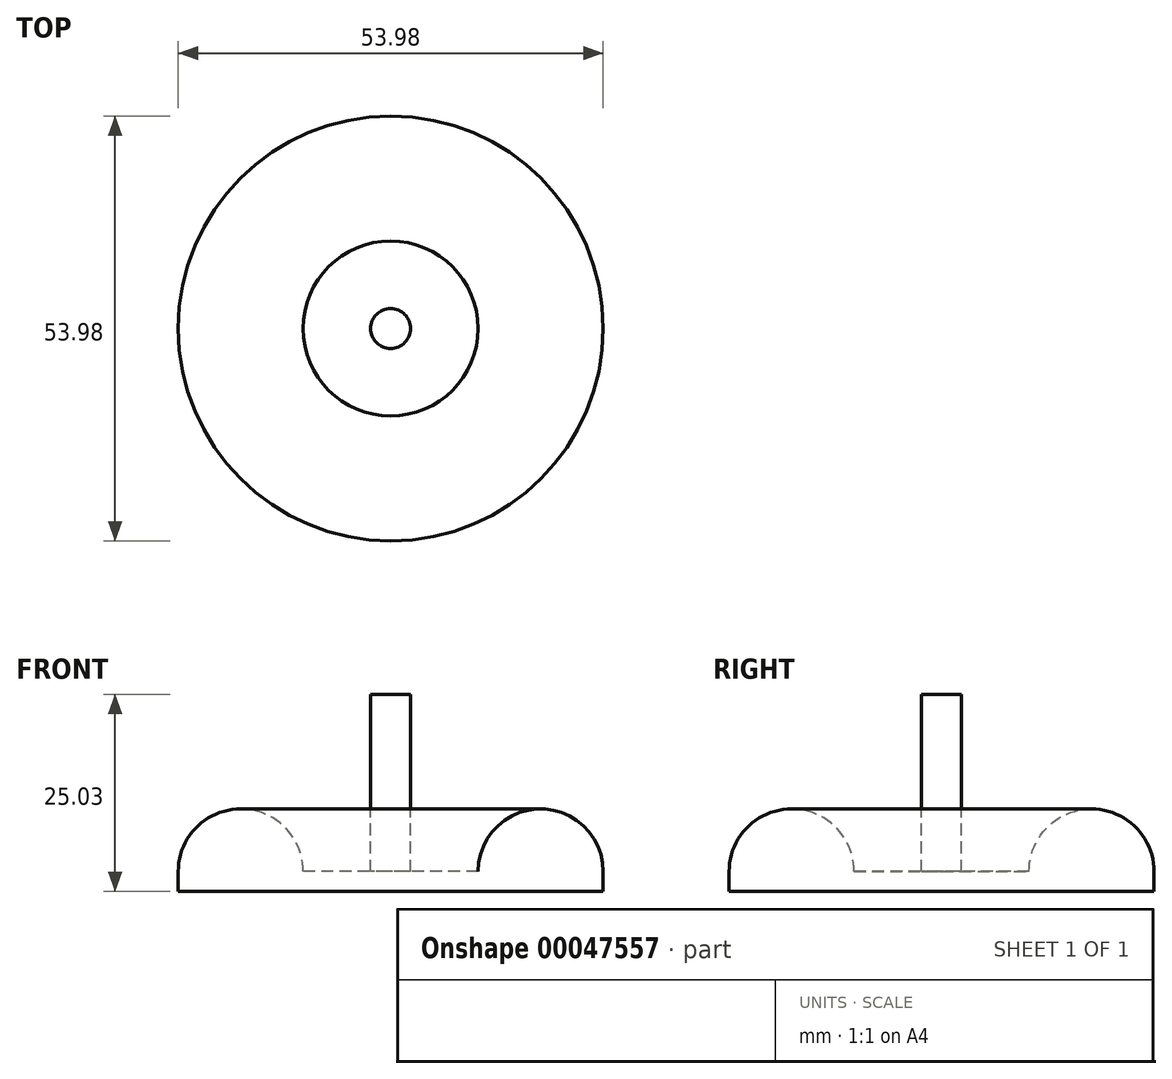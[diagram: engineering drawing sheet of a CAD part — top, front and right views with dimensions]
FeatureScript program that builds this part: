
annotation { "Feature Type Name" : "Feature", "Feature Type Description" : "" }
export const myFeature = defineFeature(function(context is Context, id is Id, definition is map)
    precondition{}
    {
        {
            var Q0;
            Q0=qCreatedBy(makeId("Front.planeOp"),FACE);
            var sketch = newSketch(context, id + "F0", { "sketchPlane" : qUnion([Q0])});
            skLineSegment(sketch, "E0", {"start": v(0, 25.03) * mm, "end": v(0, -15.1) * mm});
            skLineSegment(sketch, "E1", {"start": v(0, 25.03) * mm, "end": v(2.54, 25.03) * mm});
            skLineSegment(sketch, "E2", {"start": v(2.54, 25.03) * mm, "end": v(2.54, 2.54) * mm});
            skLineSegment(sketch, "E3", {"start": v(2.54, 2.54) * mm, "end": v(11.11, 2.54) * mm});
            skArc(sketch, "E4", {"start": v(26.99, 2.54) * mm, "mid": v(19.05, 10.48) * mm, "end": v(11.11, 2.54) * mm});
            skLineSegment(sketch, "E5", {"start": v(26.99, 2.54) * mm, "end": v(26.99, 0) * mm});
            skLineSegment(sketch, "E6", {"start": v(26.99, 0) * mm, "end": v(0, 0) * mm});
            skSolve(sketch);
        }
        {
            var Q0;
            {var subQ2=sQuery(id+"F0.wireOp",EDGE,"E1");Q0=makeQuery(id+"F0.imprint","IMPRINT",FACE,{"disambiguationData":[TD([[makeQuery(id+"F0.imprint","IMPRINT",EDGE,{"derivedFrom":subQ2}),-1.0]])]});}
            var Q1;
            Q1=sQuery(id+"F0.wireOp",EDGE,"E0");
            revolve(context, id + "F1", {"entities" : qUnion([Q0]), "axis" : qUnion([Q1]), "revolveType" : RevolveType.FULL});
        }
    });
